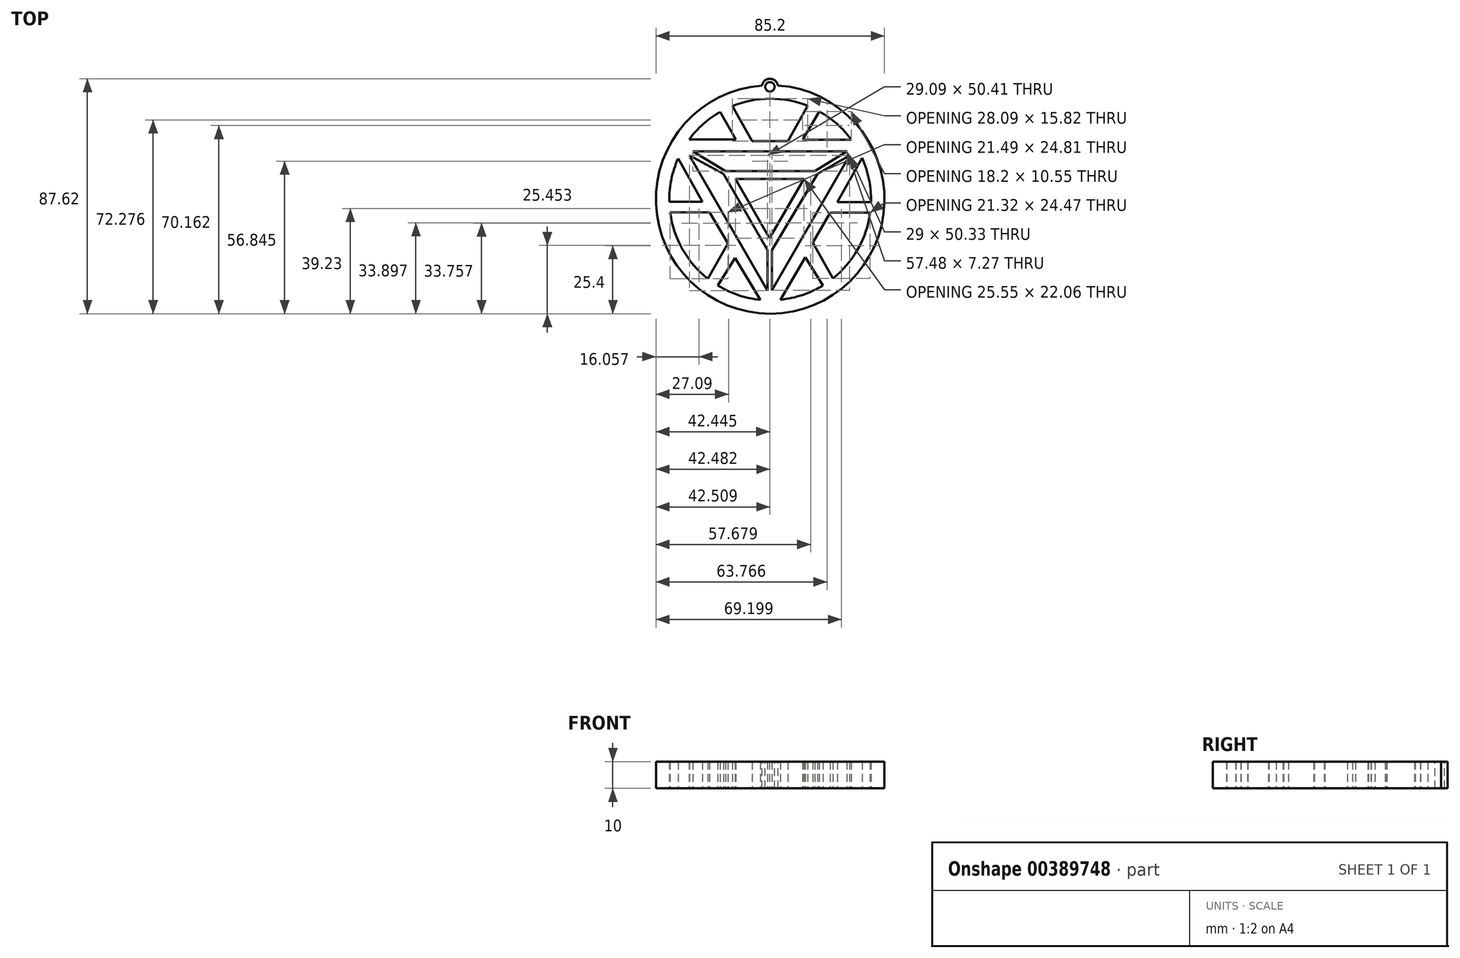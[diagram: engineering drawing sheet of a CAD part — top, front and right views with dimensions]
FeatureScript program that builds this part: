
annotation { "Feature Type Name" : "Feature", "Feature Type Description" : "" }
export const myFeature = defineFeature(function(context is Context, id is Id, definition is map)
    precondition{}
    {
        {
            var Q0;
            Q0=qCreatedBy(makeId("Top.planeOp"),FACE);
            var sketch = newSketch(context, id + "F0", { "sketchPlane" : qUnion([Q0])});
            skLineSegment(sketch, "E0", {"start": v(-16.42, 11.04) * mm, "end": v(9.13, 11.04) * mm});
            skLineSegment(sketch, "E1", {"start": v(9.13, 11.04) * mm, "end": v(-3.7, -11.02) * mm});
            skLineSegment(sketch, "E2", {"start": v(-3.7, -11.02) * mm, "end": v(-16.42, 11.04) * mm});
            skLineSegment(sketch, "E3", {"start": v(-32.35, 21.26) * mm, "end": v(25.13, 21.26) * mm});
            skLineSegment(sketch, "E4", {"start": v(25.13, 21.26) * mm, "end": v(13.18, 13.99) * mm});
            skLineSegment(sketch, "E5", {"start": v(13.18, 13.99) * mm, "end": v(-20.09, 13.99) * mm});
            skLineSegment(sketch, "E6", {"start": v(-20.09, 13.99) * mm, "end": v(-32.35, 21.26) * mm});
            skLineSegment(sketch, "E7", {"start": v(14.16, 12.94) * mm, "end": v(26.1, 19.84) * mm});
            skLineSegment(sketch, "E8", {"start": v(26.1, 19.84) * mm, "end": v(-2.91, -30.49) * mm});
            skLineSegment(sketch, "E9", {"start": v(-2.91, -30.49) * mm, "end": v(-2.91, -15.5) * mm});
            skLineSegment(sketch, "E10", {"start": v(-33.54, 19.74) * mm, "end": v(-4.46, -30.67) * mm});
            skLineSegment(sketch, "E11", {"start": v(-4.46, -30.67) * mm, "end": v(-4.46, -15.57) * mm});
            skLineSegment(sketch, "E12", {"start": v(-4.46, -15.57) * mm, "end": v(-20.9, 12.94) * mm});
            skLineSegment(sketch, "E13", {"start": v(-20.9, 12.94) * mm, "end": v(-33.54, 19.74) * mm});
            skLineSegment(sketch, "E14", {"start": v(14.16, 12.94) * mm, "end": v(-2.91, -15.5) * mm});
            skLineSegment(sketch, "E15", {"start": v(12.45, -12.69) * mm, "end": v(18.9, -1.58) * mm});
            skLineSegment(sketch, "E16", {"start": v(18.9, -1.58) * mm, "end": v(33.77, -1.58) * mm});
            skLineSegment(sketch, "E17", {"start": v(12.45, -12.69) * mm, "end": v(19.88, -26.06) * mm});
            skLineSegment(sketch, "E18", {"start": v(34.08, 2.35) * mm, "end": v(21.47, 2.35) * mm});
            skLineSegment(sketch, "E19", {"start": v(21.47, 2.35) * mm, "end": v(30.77, 18.84) * mm});
            skLineSegment(sketch, "E20", {"start": v(0.32, -34.01) * mm, "end": v(9.57, -18.15) * mm});
            skLineSegment(sketch, "E21", {"start": v(9.57, -18.15) * mm, "end": v(16.17, -28.66) * mm});
            skLineSegment(sketch, "E22", {"start": v(-23, -28.75) * mm, "end": v(-16.58, -18.42) * mm});
            skLineSegment(sketch, "E23", {"start": v(-16.58, -18.42) * mm, "end": v(-7.16, -34.03) * mm});
            skLineSegment(sketch, "E24", {"start": v(-40.78, -1.36) * mm, "end": v(-26.05, -1.36) * mm});
            skLineSegment(sketch, "E25", {"start": v(-26.05, -1.36) * mm, "end": v(-19.29, -13) * mm});
            skLineSegment(sketch, "E26", {"start": v(-19.29, -13) * mm, "end": v(-26.72, -26.17) * mm});
            skLineSegment(sketch, "E27", {"start": v(-37.83, 18.66) * mm, "end": v(-28.7, 2.56) * mm});
            skLineSegment(sketch, "E28", {"start": v(-28.7, 2.56) * mm, "end": v(-41.07, 2.56) * mm});
            skLineSegment(sketch, "E29", {"start": v(-17.63, 38.2) * mm, "end": v(-10.26, 25.14) * mm});
            skLineSegment(sketch, "E30", {"start": v(-10.26, 25.14) * mm, "end": v(3.08, 25.14) * mm});
            skLineSegment(sketch, "E31", {"start": v(3.08, 25.14) * mm, "end": v(10.47, 38.29) * mm});
            skLineSegment(sketch, "E32", {"start": v(-33.71, 25.73) * mm, "end": v(-16.34, 25.73) * mm});
            skLineSegment(sketch, "E33", {"start": v(-16.34, 25.73) * mm, "end": v(-22.12, 36.03) * mm});
            skLineSegment(sketch, "E34", {"start": v(26.77, 25.67) * mm, "end": v(8.58, 25.67) * mm});
            skLineSegment(sketch, "E35", {"start": v(8.58, 25.67) * mm, "end": v(14.8, 36.21) * mm});
            skArc(sketch, "E36", {"start": v(19.88, -26.06) * mm, "mid": v(29.2, -15.17) * mm, "end": v(33.77, -1.58) * mm});
            skArc(sketch, "E37.trimOffspring", {"start": v(0.32, -34.01) * mm, "mid": v(8.55, -32.23) * mm, "end": v(16.17, -28.66) * mm});
            skArc(sketch, "E38.trimOffspring", {"start": v(-23, -28.75) * mm, "mid": v(-15.38, -32.28) * mm, "end": v(-7.16, -34.03) * mm});
            skArc(sketch, "E39.trimOffspring", {"start": v(10.47, 38.28) * mm, "mid": v(-3.59, 40.97) * mm, "end": v(-17.63, 38.2) * mm});
            skArc(sketch, "E40.trimOffspring", {"start": v(-22.12, 36.03) * mm, "mid": v(-28.45, 31.48) * mm, "end": v(-33.71, 25.73) * mm});
            skArc(sketch, "E41.trimOffspring", {"start": v(-37.83, 18.66) * mm, "mid": v(-40.34, 10.8) * mm, "end": v(-41.07, 2.56) * mm});
            skArc(sketch, "E42.trimOffspring", {"start": v(26.77, 25.67) * mm, "mid": v(21.35, 31.58) * mm, "end": v(14.8, 36.21) * mm});
            skArc(sketch, "E43.trimOffspring", {"start": v(34.08, 2.35) * mm, "mid": v(33.36, 10.79) * mm, "end": v(30.77, 18.84) * mm});
            skArc(sketch, "E44.trimOffspring", {"start": v(-40.78, -1.36) * mm, "mid": v(-36.2, -15.15) * mm, "end": v(-26.72, -26.17) * mm});
            skPoint(sketch, "E45.centerSnap0", {"position": v(-3.46, 13.99) * mm});
            skPoint(sketch, "E46.centerSnap0", {"position": v(-3.6, 25.14) * mm});
            skCircle(sketch, "E47.0", {"center": v(-3.5, 3.38) * mm, "radius": 42.6 * mm});
            skSolve(sketch);
        }
        {
            var Q0;
            Q0 = qSketchRegion(id + "F0", true);
            extrude(context, id + "F1", {"entities" : qUnion([Q0]), "depth" : 10 * mm});
        }
        {
            var Q0;
            Q0=makeQuery(id+"F1.opExtrude","CAP_FACE",FACE,{"disambiguationData":[OSD([sQuery(id+"F0.wireOp",EDGE,"E0"),sQuery(id+"F0.wireOp",EDGE,"E1"),sQuery(id+"F0.wireOp",EDGE,"E2"),sQuery(id+"F0.wireOp",EDGE,"E3"),sQuery(id+"F0.wireOp",EDGE,"E4"),sQuery(id+"F0.wireOp",EDGE,"E5"),sQuery(id+"F0.wireOp",EDGE,"E6"),sQuery(id+"F0.wireOp",EDGE,"E7"),sQuery(id+"F0.wireOp",EDGE,"E8"),sQuery(id+"F0.wireOp",EDGE,"E9"),sQuery(id+"F0.wireOp",EDGE,"E10"),sQuery(id+"F0.wireOp",EDGE,"E11"),sQuery(id+"F0.wireOp",EDGE,"E12"),sQuery(id+"F0.wireOp",EDGE,"E13"),sQuery(id+"F0.wireOp",EDGE,"E14"),sQuery(id+"F0.wireOp",EDGE,"E15"),sQuery(id+"F0.wireOp",EDGE,"E16"),sQuery(id+"F0.wireOp",EDGE,"E17"),sQuery(id+"F0.wireOp",EDGE,"E18"),sQuery(id+"F0.wireOp",EDGE,"E19"),sQuery(id+"F0.wireOp",EDGE,"E20"),sQuery(id+"F0.wireOp",EDGE,"E21"),sQuery(id+"F0.wireOp",EDGE,"E22"),sQuery(id+"F0.wireOp",EDGE,"E23"),sQuery(id+"F0.wireOp",EDGE,"E24"),sQuery(id+"F0.wireOp",EDGE,"E25"),sQuery(id+"F0.wireOp",EDGE,"E26"),sQuery(id+"F0.wireOp",EDGE,"E27"),sQuery(id+"F0.wireOp",EDGE,"E28"),sQuery(id+"F0.wireOp",EDGE,"E29"),sQuery(id+"F0.wireOp",EDGE,"E30"),sQuery(id+"F0.wireOp",EDGE,"E31"),sQuery(id+"F0.wireOp",EDGE,"E32"),sQuery(id+"F0.wireOp",EDGE,"E33"),sQuery(id+"F0.wireOp",EDGE,"E34"),sQuery(id+"F0.wireOp",EDGE,"E35"),sQuery(id+"F0.wireOp",EDGE,"E36"),sQuery(id+"F0.wireOp",EDGE,"E37.trimOffspring"),sQuery(id+"F0.wireOp",EDGE,"E38.trimOffspring"),sQuery(id+"F0.wireOp",EDGE,"E39.trimOffspring"),sQuery(id+"F0.wireOp",EDGE,"E40.trimOffspring"),sQuery(id+"F0.wireOp",EDGE,"E41.trimOffspring"),sQuery(id+"F0.wireOp",EDGE,"E42.trimOffspring"),sQuery(id+"F0.wireOp",EDGE,"E43.trimOffspring"),sQuery(id+"F0.wireOp",EDGE,"E44.trimOffspring"),sQuery(id+"F0.wireOp",EDGE,"E47.0")])],"isStart":false});
            var sketch = newSketch(context, id + "F2", { "sketchPlane" : qUnion([Q0])});
            skCircle(sketch, "E48", {"center": v(-3.59, 45.4) * mm, "radius": 3 * mm});
            skPoint(sketch, "E48.centerSnap0", {"position": v(-3.59, 40.97) * mm});
            skSolve(sketch);
        }
        {
            var Q0;
            Q0 = qSketchRegion(id + "F2", true);
            var Q1;
            Q1=makeQuery(id+"F1.opExtrude","CAP_FACE",FACE,{"disambiguationData":[OSD([sQuery(id+"F0.wireOp",EDGE,"E0"),sQuery(id+"F0.wireOp",EDGE,"E1"),sQuery(id+"F0.wireOp",EDGE,"E2"),sQuery(id+"F0.wireOp",EDGE,"E3"),sQuery(id+"F0.wireOp",EDGE,"E4"),sQuery(id+"F0.wireOp",EDGE,"E5"),sQuery(id+"F0.wireOp",EDGE,"E6"),sQuery(id+"F0.wireOp",EDGE,"E7"),sQuery(id+"F0.wireOp",EDGE,"E8"),sQuery(id+"F0.wireOp",EDGE,"E9"),sQuery(id+"F0.wireOp",EDGE,"E10"),sQuery(id+"F0.wireOp",EDGE,"E11"),sQuery(id+"F0.wireOp",EDGE,"E12"),sQuery(id+"F0.wireOp",EDGE,"E13"),sQuery(id+"F0.wireOp",EDGE,"E14"),sQuery(id+"F0.wireOp",EDGE,"E15"),sQuery(id+"F0.wireOp",EDGE,"E16"),sQuery(id+"F0.wireOp",EDGE,"E17"),sQuery(id+"F0.wireOp",EDGE,"E18"),sQuery(id+"F0.wireOp",EDGE,"E19"),sQuery(id+"F0.wireOp",EDGE,"E20"),sQuery(id+"F0.wireOp",EDGE,"E21"),sQuery(id+"F0.wireOp",EDGE,"E22"),sQuery(id+"F0.wireOp",EDGE,"E23"),sQuery(id+"F0.wireOp",EDGE,"E24"),sQuery(id+"F0.wireOp",EDGE,"E25"),sQuery(id+"F0.wireOp",EDGE,"E26"),sQuery(id+"F0.wireOp",EDGE,"E27"),sQuery(id+"F0.wireOp",EDGE,"E28"),sQuery(id+"F0.wireOp",EDGE,"E29"),sQuery(id+"F0.wireOp",EDGE,"E30"),sQuery(id+"F0.wireOp",EDGE,"E31"),sQuery(id+"F0.wireOp",EDGE,"E32"),sQuery(id+"F0.wireOp",EDGE,"E33"),sQuery(id+"F0.wireOp",EDGE,"E34"),sQuery(id+"F0.wireOp",EDGE,"E35"),sQuery(id+"F0.wireOp",EDGE,"E36"),sQuery(id+"F0.wireOp",EDGE,"E37.trimOffspring"),sQuery(id+"F0.wireOp",EDGE,"E38.trimOffspring"),sQuery(id+"F0.wireOp",EDGE,"E39.trimOffspring"),sQuery(id+"F0.wireOp",EDGE,"E40.trimOffspring"),sQuery(id+"F0.wireOp",EDGE,"E41.trimOffspring"),sQuery(id+"F0.wireOp",EDGE,"E42.trimOffspring"),sQuery(id+"F0.wireOp",EDGE,"E43.trimOffspring"),sQuery(id+"F0.wireOp",EDGE,"E44.trimOffspring"),sQuery(id+"F0.wireOp",EDGE,"E47.0")])],"isStart":true});
            extrude(context, id + "F3", {"entities" : qUnion([Q0]), "operationType" : NewBodyOperationType.ADD, "endBound" : BoundingType.UP_TO_SURFACE, "oppositeDirection" : true, "endBoundEntityFace" : qUnion([Q1]), "depth" : 25 * mm});
        }
        {
            var Q0;
            Q0=makeQuery(id+"F3.boolean.opBoolean","MERGE",FACE,{"derivedFrom":[makeQuery(id+"F1.opExtrude","CAP_FACE",FACE,{"disambiguationData":[OSD([sQuery(id+"F0.wireOp",EDGE,"E0"),sQuery(id+"F0.wireOp",EDGE,"E1"),sQuery(id+"F0.wireOp",EDGE,"E2"),sQuery(id+"F0.wireOp",EDGE,"E3"),sQuery(id+"F0.wireOp",EDGE,"E4"),sQuery(id+"F0.wireOp",EDGE,"E5"),sQuery(id+"F0.wireOp",EDGE,"E6"),sQuery(id+"F0.wireOp",EDGE,"E7"),sQuery(id+"F0.wireOp",EDGE,"E8"),sQuery(id+"F0.wireOp",EDGE,"E9"),sQuery(id+"F0.wireOp",EDGE,"E10"),sQuery(id+"F0.wireOp",EDGE,"E11"),sQuery(id+"F0.wireOp",EDGE,"E12"),sQuery(id+"F0.wireOp",EDGE,"E13"),sQuery(id+"F0.wireOp",EDGE,"E14"),sQuery(id+"F0.wireOp",EDGE,"E15"),sQuery(id+"F0.wireOp",EDGE,"E16"),sQuery(id+"F0.wireOp",EDGE,"E17"),sQuery(id+"F0.wireOp",EDGE,"E18"),sQuery(id+"F0.wireOp",EDGE,"E19"),sQuery(id+"F0.wireOp",EDGE,"E20"),sQuery(id+"F0.wireOp",EDGE,"E21"),sQuery(id+"F0.wireOp",EDGE,"E22"),sQuery(id+"F0.wireOp",EDGE,"E23"),sQuery(id+"F0.wireOp",EDGE,"E24"),sQuery(id+"F0.wireOp",EDGE,"E25"),sQuery(id+"F0.wireOp",EDGE,"E26"),sQuery(id+"F0.wireOp",EDGE,"E27"),sQuery(id+"F0.wireOp",EDGE,"E28"),sQuery(id+"F0.wireOp",EDGE,"E29"),sQuery(id+"F0.wireOp",EDGE,"E30"),sQuery(id+"F0.wireOp",EDGE,"E31"),sQuery(id+"F0.wireOp",EDGE,"E32"),sQuery(id+"F0.wireOp",EDGE,"E33"),sQuery(id+"F0.wireOp",EDGE,"E34"),sQuery(id+"F0.wireOp",EDGE,"E35"),sQuery(id+"F0.wireOp",EDGE,"E36"),sQuery(id+"F0.wireOp",EDGE,"E37.trimOffspring"),sQuery(id+"F0.wireOp",EDGE,"E38.trimOffspring"),sQuery(id+"F0.wireOp",EDGE,"E39.trimOffspring"),sQuery(id+"F0.wireOp",EDGE,"E40.trimOffspring"),sQuery(id+"F0.wireOp",EDGE,"E41.trimOffspring"),sQuery(id+"F0.wireOp",EDGE,"E42.trimOffspring"),sQuery(id+"F0.wireOp",EDGE,"E43.trimOffspring"),sQuery(id+"F0.wireOp",EDGE,"E44.trimOffspring"),sQuery(id+"F0.wireOp",EDGE,"E47.0")])],"isStart":false}),makeQuery(id+"F3.opExtrude","CAP_FACE",FACE,{"disambiguationData":[OSD([sQuery(id+"F2.wireOp",EDGE,"E48")])],"isStart":true})]});
            var sketch = newSketch(context, id + "F4", { "sketchPlane" : qUnion([Q0])});
            skCircle(sketch, "E49", {"center": v(-3.59, 45.4) * mm, "radius": 1.75 * mm});
            skSolve(sketch);
        }
        {
            var Q0;
            Q0 = qSketchRegion(id + "F4", true);
            var Q1;
            {var subQ0=sQuery(id+"F0.wireOp",EDGE,"E47.0");var subQ1=sQuery(id+"F0.wireOp",EDGE,"E44.trimOffspring");var subQ2=sQuery(id+"F0.wireOp",EDGE,"E43.trimOffspring");var subQ3=sQuery(id+"F0.wireOp",EDGE,"E42.trimOffspring");var subQ4=sQuery(id+"F0.wireOp",EDGE,"E41.trimOffspring");var subQ5=sQuery(id+"F0.wireOp",EDGE,"E40.trimOffspring");var subQ6=sQuery(id+"F0.wireOp",EDGE,"E39.trimOffspring");var subQ7=sQuery(id+"F0.wireOp",EDGE,"E38.trimOffspring");var subQ8=sQuery(id+"F0.wireOp",EDGE,"E37.trimOffspring");var subQ9=sQuery(id+"F0.wireOp",EDGE,"E36");var subQ10=sQuery(id+"F0.wireOp",EDGE,"E35");var subQ11=sQuery(id+"F0.wireOp",EDGE,"E34");var subQ12=sQuery(id+"F0.wireOp",EDGE,"E33");var subQ13=sQuery(id+"F0.wireOp",EDGE,"E32");var subQ14=sQuery(id+"F0.wireOp",EDGE,"E31");var subQ15=sQuery(id+"F0.wireOp",EDGE,"E30");var subQ16=sQuery(id+"F0.wireOp",EDGE,"E29");var subQ17=sQuery(id+"F0.wireOp",EDGE,"E28");var subQ18=sQuery(id+"F0.wireOp",EDGE,"E27");var subQ19=sQuery(id+"F0.wireOp",EDGE,"E26");var subQ20=sQuery(id+"F0.wireOp",EDGE,"E25");var subQ21=sQuery(id+"F0.wireOp",EDGE,"E24");var subQ22=sQuery(id+"F0.wireOp",EDGE,"E23");var subQ23=sQuery(id+"F0.wireOp",EDGE,"E22");var subQ24=sQuery(id+"F0.wireOp",EDGE,"E21");var subQ25=sQuery(id+"F0.wireOp",EDGE,"E20");var subQ26=sQuery(id+"F0.wireOp",EDGE,"E19");var subQ27=sQuery(id+"F0.wireOp",EDGE,"E18");var subQ28=sQuery(id+"F0.wireOp",EDGE,"E17");var subQ29=sQuery(id+"F0.wireOp",EDGE,"E16");var subQ30=sQuery(id+"F0.wireOp",EDGE,"E15");var subQ31=sQuery(id+"F0.wireOp",EDGE,"E14");var subQ32=sQuery(id+"F0.wireOp",EDGE,"E13");var subQ33=sQuery(id+"F0.wireOp",EDGE,"E12");var subQ34=sQuery(id+"F0.wireOp",EDGE,"E11");var subQ35=sQuery(id+"F0.wireOp",EDGE,"E10");var subQ36=sQuery(id+"F0.wireOp",EDGE,"E9");var subQ37=sQuery(id+"F0.wireOp",EDGE,"E8");var subQ38=sQuery(id+"F0.wireOp",EDGE,"E7");var subQ39=sQuery(id+"F0.wireOp",EDGE,"E6");var subQ40=sQuery(id+"F0.wireOp",EDGE,"E5");var subQ41=sQuery(id+"F0.wireOp",EDGE,"E4");var subQ42=sQuery(id+"F0.wireOp",EDGE,"E3");var subQ43=sQuery(id+"F0.wireOp",EDGE,"E2");var subQ44=sQuery(id+"F0.wireOp",EDGE,"E1");var subQ45=sQuery(id+"F0.wireOp",EDGE,"E0");Q1=makeQuery(id+"F3.boolean.opBoolean","MERGE",FACE,{"derivedFrom":[makeQuery(id+"F1.opExtrude","CAP_FACE",FACE,{"disambiguationData":[OSD([subQ45,subQ44,subQ43,subQ42,subQ41,subQ40,subQ39,subQ38,subQ37,subQ36,subQ35,subQ34,subQ33,subQ32,subQ31,subQ30,subQ29,subQ28,subQ27,subQ26,subQ25,subQ24,subQ23,subQ22,subQ21,subQ20,subQ19,subQ18,subQ17,subQ16,subQ15,subQ14,subQ13,subQ12,subQ11,subQ10,subQ9,subQ8,subQ7,subQ6,subQ5,subQ4,subQ3,subQ2,subQ1,subQ0])],"isStart":true}),makeQuery(id+"F3.opExtrude","CAP_FACE",FACE,{"disambiguationData":[OSD([subQ45,subQ44,subQ43,subQ42,subQ41,subQ40,subQ39,subQ38,subQ37,subQ36,subQ35,subQ34,subQ33,subQ32,subQ31,subQ30,subQ29,subQ28,subQ27,subQ26,subQ25,subQ24,subQ23,subQ22,subQ21,subQ20,subQ19,subQ18,subQ17,subQ16,subQ15,subQ14,subQ13,subQ12,subQ11,subQ10,subQ9,subQ8,subQ7,subQ6,subQ5,subQ4,subQ3,subQ2,subQ1,subQ0])],"isStart":false})]});}
            extrude(context, id + "F5", {"entities" : qUnion([Q0]), "operationType" : NewBodyOperationType.REMOVE, "endBound" : BoundingType.UP_TO_SURFACE, "oppositeDirection" : true, "endBoundEntityFace" : qUnion([Q1]), "depth" : 25 * mm});
        }
    });
